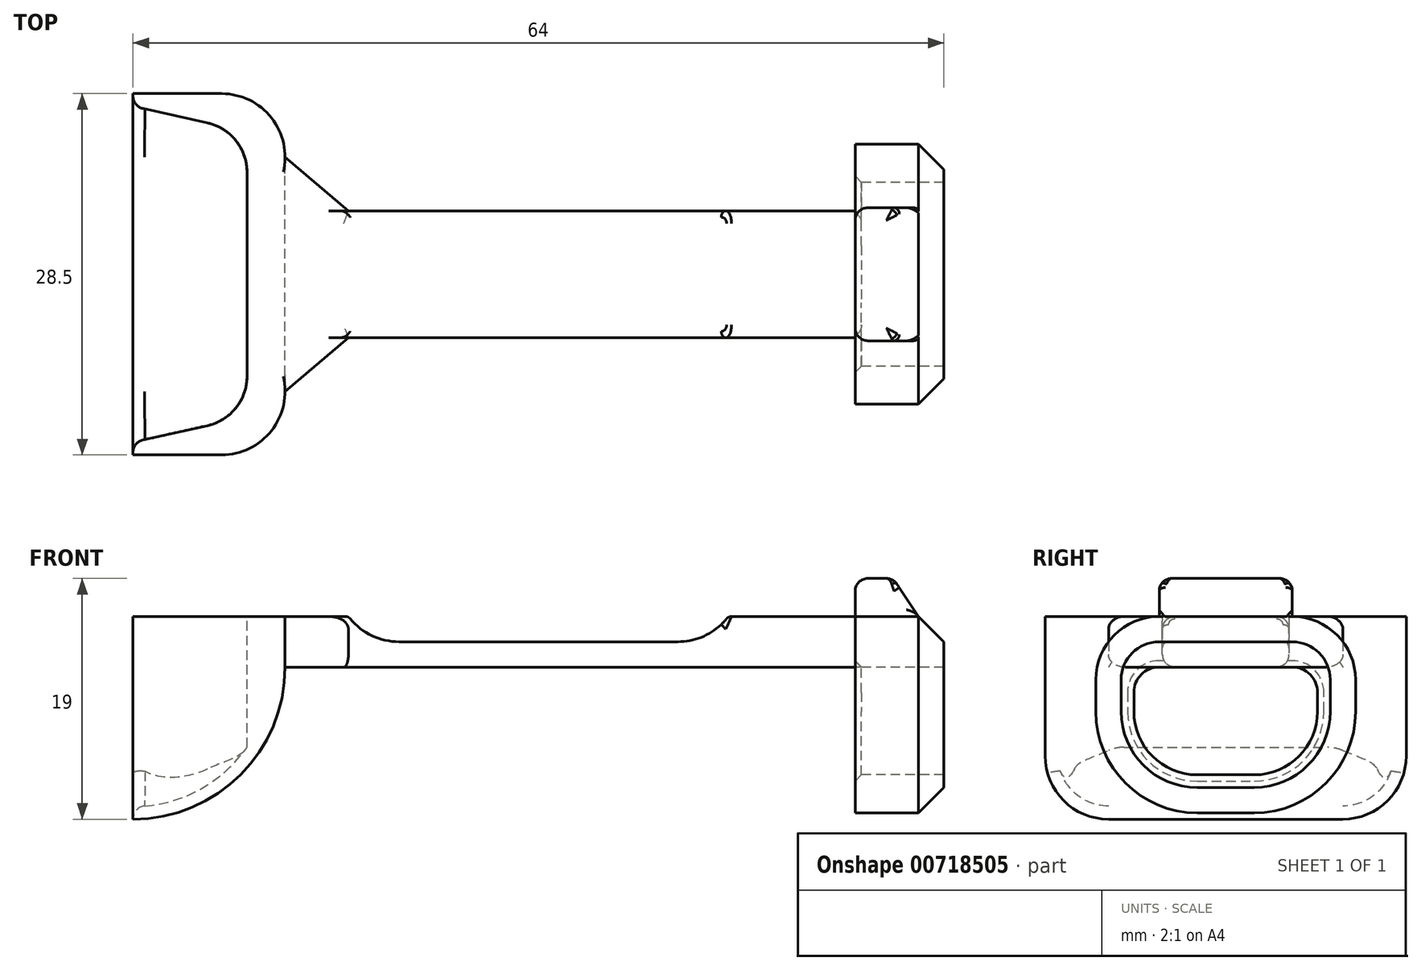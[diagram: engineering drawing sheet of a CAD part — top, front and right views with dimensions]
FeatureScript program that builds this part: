
annotation { "Feature Type Name" : "Feature", "Feature Type Description" : "" }
export const myFeature = defineFeature(function(context is Context, id is Id, definition is map)
    precondition{}
    {
        {
            assignVariable(context, id + "F0", {"variableType" : VariableType.LENGTH, "name" : "ScoopHeight", "lengthValue" : 12 * mm});
        }
        {
            assignVariable(context, id + "F1", {"variableType" : VariableType.LENGTH, "name" : "Length", "lengthValue" : 40 * mm});
        }
        {
            assignVariable(context, id + "F2", {"variableType" : VariableType.LENGTH, "name" : "OverHeight", "lengthValue" : 4 * mm});
        }
        {
            assignVariable(context, id + "F3", {"variableType" : VariableType.LENGTH, "name" : "BraceLength", "lengthValue" : 7 * mm});
        }
        {
            assignVariable(context, id + "F4", {"variableType" : VariableType.LENGTH, "name" : "StartLength", "lengthValue" : 5 * mm});
        }
        {
            var Q0;
            Q0=qCreatedBy(makeId("Right.planeOp"),FACE);
            var sketch = newSketch(context, id + "F5", { "sketchPlane" : qUnion([Q0])});
            skLineSegment(sketch, "E0", {"start": v(0, 0) * mm, "end": v(9.25, 0) * mm});
            skLineSegment(sketch, "E1", {"start": v(14.25, 5) * mm, "end": v(14.25, 12) * mm});
            skLineSegment(sketch, "E2", {"start": v(14.25, 12) * mm, "end": v(13.25, 12) * mm});
            skLineSegment(sketch, "E3", {"start": v(13.25, 12) * mm, "end": v(13.25, 5) * mm});
            skLineSegment(sketch, "E4", {"start": v(9.25, 1) * mm, "end": v(-9.25, 1) * mm});
            skLineSegment(sketch, "E5", {"start": v(-13.25, 5) * mm, "end": v(-13.25, 12) * mm});
            skLineSegment(sketch, "E6", {"start": v(-13.25, 12) * mm, "end": v(-14.25, 12) * mm});
            skLineSegment(sketch, "E7", {"start": v(-14.25, 12) * mm, "end": v(-14.25, 5) * mm});
            skLineSegment(sketch, "E8", {"start": v(-9.25, 0) * mm, "end": v(0, 0) * mm});
            skLineSegment(sketch, "E9", {"start": v(3.93, 12) * mm, "end": v(-6.74, 12) * mm});
            skPoint(sketch, "E10.visualSharp", {"position": v(13.25, 1) * mm});
            skArc(sketch, "E10.filletArc", {"start": v(9.25, 1) * mm, "mid": v(12.08, 2.17) * mm, "end": v(13.25, 5) * mm});
            skPoint(sketch, "E11.visualSharp", {"position": v(-13.25, 1) * mm});
            skArc(sketch, "E11.filletArc", {"start": v(-13.25, 5) * mm, "mid": v(-12.08, 2.17) * mm, "end": v(-9.25, 1) * mm});
            skPoint(sketch, "E12.visualSharp", {"position": v(-14.25, 0) * mm});
            skArc(sketch, "E12.filletArc", {"start": v(-14.25, 5) * mm, "mid": v(-12.79, 1.46) * mm, "end": v(-9.25, 0) * mm});
            skPoint(sketch, "E13.visualSharp", {"position": v(14.25, 0) * mm});
            skArc(sketch, "E13.filletArc", {"start": v(9.25, 0) * mm, "mid": v(12.79, 1.46) * mm, "end": v(14.25, 5) * mm});
            skSolve(sketch);
        }
        {
            var Q0;
            Q0=makeQuery(id+"F5.imprint","IMPRINT",FACE,{"disambiguationData":[TD([[makeQuery(id+"F5.imprint","IMPRINT",EDGE,{"derivedFrom":sQuery(id+"F5.wireOp",EDGE,"E0")}),1.0]])]});
            var Q1;
            Q1=sQuery(id+"F5.wireOp",EDGE,"E9");
            revolve(context, id + "F6", {"surfaceOperationType" : NewSurfaceOperationType.NEW, "entities" : qUnion([Q0]), "axis" : qUnion([Q1]), "revolveType" : RevolveType.ONE_DIRECTION, "angle" : 90 * degree});
        }
        {
            var Q0;
            Q0=makeQuery(id+"F6.opRevolve","CAP_FACE",FACE,{"disambiguationData":[OSD([sQuery(id+"F5.wireOp",EDGE,"E0"),sQuery(id+"F5.wireOp",EDGE,"E1"),sQuery(id+"F5.wireOp",EDGE,"E2"),sQuery(id+"F5.wireOp",EDGE,"E3"),sQuery(id+"F5.wireOp",EDGE,"E4"),sQuery(id+"F5.wireOp",EDGE,"E5"),sQuery(id+"F5.wireOp",EDGE,"E6"),sQuery(id+"F5.wireOp",EDGE,"E7"),sQuery(id+"F5.wireOp",EDGE,"E8"),sQuery(id+"F5.wireOp",EDGE,"E10.filletArc"),sQuery(id+"F5.wireOp",EDGE,"E11.filletArc"),sQuery(id+"F5.wireOp",EDGE,"E12.filletArc"),sQuery(id+"F5.wireOp",EDGE,"E13.filletArc")])],"isStart":false});
            var sketch = newSketch(context, id + "F7", { "sketchPlane" : qUnion([Q0])});
            skLineSegment(sketch, "E14", {"start": v(9, -8.04) * mm, "end": v(9, 8.04) * mm});
            skLineSegment(sketch, "E15", {"start": v(5.87, -11.95) * mm, "end": v(0, -13.25) * mm});
            skLineSegment(sketch, "E16", {"start": v(5.87, 11.95) * mm, "end": v(0, 13.25) * mm});
            skPoint(sketch, "E17.visualSharp", {"position": v(9, 11.25) * mm});
            skArc(sketch, "E17.filletArc", {"start": v(9, 8.04) * mm, "mid": v(8.12, 10.54) * mm, "end": v(5.87, 11.95) * mm});
            skPoint(sketch, "E18.visualSharp", {"position": v(9, -11.25) * mm});
            skArc(sketch, "E18.filletArc", {"start": v(5.87, -11.95) * mm, "mid": v(8.12, -10.54) * mm, "end": v(9, -8.04) * mm});
            skSolve(sketch);
        }
        {
            var Q0;
            Q0=makeQuery(id+"F7.imprint","IMPRINT",FACE,{"disambiguationData":[TD([[makeQuery(id+"F7.imprint","IMPRINT",EDGE,{"derivedFrom":sQuery(id+"F7.wireOp",EDGE,"E14")}),-1.0]])]});
            extrude(context, id + "F8", {"entities" : qUnion([Q0]), "operationType" : NewBodyOperationType.ADD, "oppositeDirection" : true, "depth" : 4 * mm, "offsetDistance" : 25 * mm});
        }
        {
            var Q0;
            Q0=makeQuery(id+"F8.opExtrude","CAP_FACE",FACE,{"disambiguationData":[OSD([sQuery(id+"F5.wireOp",EDGE,"E3"),sQuery(id+"F5.wireOp",EDGE,"E4"),sQuery(id+"F5.wireOp",EDGE,"E5"),sQuery(id+"F5.wireOp",EDGE,"E10.filletArc"),sQuery(id+"F5.wireOp",EDGE,"E11.filletArc"),sQuery(id+"F7.wireOp",EDGE,"E14"),sQuery(id+"F7.wireOp",EDGE,"E15"),sQuery(id+"F7.wireOp",EDGE,"E16"),sQuery(id+"F7.wireOp",EDGE,"E17.filletArc"),sQuery(id+"F7.wireOp",EDGE,"E18.filletArc")])],"isStart":false});
            extrude(context, id + "F9", {"entities" : qUnion([Q0]), "operationType" : NewBodyOperationType.ADD, "depth" : 2 * mm, "offsetDistance" : 25 * mm});
        }
        {
            var Q0;
            Q0=makeQuery(id+"F9.opExtrude","CAP_FACE",FACE,{"disambiguationData":[OSD([sQuery(id+"F5.wireOp",EDGE,"E3"),sQuery(id+"F5.wireOp",EDGE,"E4"),sQuery(id+"F5.wireOp",EDGE,"E5"),sQuery(id+"F5.wireOp",EDGE,"E10.filletArc"),sQuery(id+"F5.wireOp",EDGE,"E11.filletArc"),sQuery(id+"F7.wireOp",EDGE,"E14"),sQuery(id+"F7.wireOp",EDGE,"E15"),sQuery(id+"F7.wireOp",EDGE,"E16"),sQuery(id+"F7.wireOp",EDGE,"E17.filletArc"),sQuery(id+"F7.wireOp",EDGE,"E18.filletArc")])],"isStart":false});
            extrude(context, id + "F10", {"entities" : qUnion([Q0]), "operationType" : NewBodyOperationType.ADD, "depth" : 1.5 * mm, "offsetDistance" : 25 * mm});
        }
        {
            var Q0;
            {var subQ0=sQuery(id+"F7.wireOp",EDGE,"E16");var subQ1=sQuery(id+"F7.wireOp",EDGE,"E17.filletArc");var subQ2=sQuery(id+"F5.wireOp",EDGE,"E10.filletArc");Q0=makeQuery(id+"F10.boolean.opBoolean","SPLIT",FACE,{"disambiguationData":[TD([makeQuery(id+"F6.opRevolve","SWEPT_FACE",FACE,{"disambiguationData":[OSD([subQ2])]})])],"derivedFrom":makeQuery(id+"F10.opExtrude","CAP_FACE",FACE,{"disambiguationData":[OSD([sQuery(id+"F5.wireOp",EDGE,"E3"),sQuery(id+"F5.wireOp",EDGE,"E4"),sQuery(id+"F5.wireOp",EDGE,"E5"),subQ2,sQuery(id+"F5.wireOp",EDGE,"E11.filletArc"),sQuery(id+"F7.wireOp",EDGE,"E14"),sQuery(id+"F7.wireOp",EDGE,"E15"),subQ0,subQ1,sQuery(id+"F7.wireOp",EDGE,"E18.filletArc")])],"isStart":false})});}
            var Q1;
            {var subQ0=sQuery(id+"F7.wireOp",EDGE,"E15");var subQ1=sQuery(id+"F7.wireOp",EDGE,"E18.filletArc");var subQ2=sQuery(id+"F5.wireOp",EDGE,"E11.filletArc");Q1=makeQuery(id+"F10.boolean.opBoolean","SPLIT",FACE,{"disambiguationData":[TD([makeQuery(id+"F6.opRevolve","SWEPT_FACE",FACE,{"disambiguationData":[OSD([subQ2])]})])],"derivedFrom":makeQuery(id+"F10.opExtrude","CAP_FACE",FACE,{"disambiguationData":[OSD([sQuery(id+"F5.wireOp",EDGE,"E3"),sQuery(id+"F5.wireOp",EDGE,"E4"),sQuery(id+"F5.wireOp",EDGE,"E5"),sQuery(id+"F5.wireOp",EDGE,"E10.filletArc"),subQ2,sQuery(id+"F7.wireOp",EDGE,"E14"),subQ0,sQuery(id+"F7.wireOp",EDGE,"E16"),sQuery(id+"F7.wireOp",EDGE,"E17.filletArc"),subQ1])],"isStart":false})});}
            extrude(context, id + "F11", {"entities" : qUnion([Q0, Q1]), "operationType" : NewBodyOperationType.ADD, "depth" : 1.5 * mm, "offsetDistance" : 25 * mm});
        }
        {
            var Q0;
            {var subQ0=sQuery(id+"F5.wireOp",EDGE,"E11.filletArc");var subQ1=sQuery(id+"F5.wireOp",EDGE,"E10.filletArc");var subQ2=sQuery(id+"F5.wireOp",EDGE,"E5");var subQ3=sQuery(id+"F5.wireOp",EDGE,"E4");var subQ4=sQuery(id+"F5.wireOp",EDGE,"E3");Q0=makeQuery(id+"F8.boolean.opBoolean","MERGE",FACE,{"derivedFrom":[makeQuery(id+"F6.opRevolve","CAP_FACE",FACE,{"disambiguationData":[OSD([sQuery(id+"F5.wireOp",EDGE,"E0"),sQuery(id+"F5.wireOp",EDGE,"E1"),sQuery(id+"F5.wireOp",EDGE,"E2"),subQ4,subQ3,subQ2,sQuery(id+"F5.wireOp",EDGE,"E6"),sQuery(id+"F5.wireOp",EDGE,"E7"),sQuery(id+"F5.wireOp",EDGE,"E8"),subQ1,subQ0,sQuery(id+"F5.wireOp",EDGE,"E12.filletArc"),sQuery(id+"F5.wireOp",EDGE,"E13.filletArc")])],"isStart":false}),makeQuery(id+"F8.opExtrude","CAP_FACE",FACE,{"disambiguationData":[OSD([subQ4,subQ3,subQ2,subQ1,subQ0,sQuery(id+"F7.wireOp",EDGE,"E14"),sQuery(id+"F7.wireOp",EDGE,"E15"),sQuery(id+"F7.wireOp",EDGE,"E16"),sQuery(id+"F7.wireOp",EDGE,"E17.filletArc"),sQuery(id+"F7.wireOp",EDGE,"E18.filletArc")])],"isStart":true})]});}
            extrude(context, id + "F12", {"entities" : qUnion([Q0]), "operationType" : NewBodyOperationType.ADD, "depth" : getVariable(context, 'OverHeight'), "offsetDistance" : 25 * mm});
        }
        {
            var Q0;
            Q0=qCreatedBy(makeId("Right.planeOp"),FACE);
            cPlane(context, id + "F13", {"entities" : qUnion([Q0]), "cplaneType" : CPlaneType.OFFSET, "offset" : getVariable(context, 'StartLength') + getVariable(context, 'ScoopHeight'), "width" : 150 * mm, "height" : 150 * mm});
        }
        {
            var Q0;
            Q0=qCreatedBy(id+"F13.planeOp",FACE);
            var sketch = newSketch(context, id + "F14", { "sketchPlane" : qUnion([Q0])});
            skLineSegment(sketch, "E19", {"start": v(-5, 16) * mm, "end": v(5, 16) * mm});
            skLineSegment(sketch, "E20", {"start": v(5, 16) * mm, "end": v(5, 12) * mm});
            skLineSegment(sketch, "E21", {"start": v(5, 12) * mm, "end": v(-5, 12) * mm});
            skLineSegment(sketch, "E22", {"start": v(-5, 12) * mm, "end": v(-5, 16) * mm});
            skSolve(sketch);
        }
        {
            var Q0;
            Q0=makeQuery(id+"F12.opExtrude","SWEPT_FACE",FACE,{"disambiguationData":[OSD([sQuery(id+"F5.wireOp",EDGE,"E0"),sQuery(id+"F5.wireOp",EDGE,"E8")])]});
            var Q1;
            Q1=makeQuery(id+"F14.imprint","IMPRINT",FACE,{"disambiguationData":[TD([[makeQuery(id+"F14.imprint","IMPRINT",EDGE,{"derivedFrom":sQuery(id+"F14.wireOp",EDGE,"E19")}),-1.0]])]});
            loft(context, id + "F15", {"operationType" : NewBodyOperationType.ADD, "sheetProfilesArray" : [{ "sheetProfileEntities" : qUnion([Q0]) }, { "sheetProfileEntities" : qUnion([Q1]) }]});
        }
        {
            var Q0;
            Q0=makeQuery(id+"F15.opLoft","CAP_FACE",FACE,{"disambiguationData":[OSD([makeQuery(id+"F14.imprint","IMPRINT",FACE,{"disambiguationData":[TD([[makeQuery(id+"F14.imprint","IMPRINT",EDGE,{"derivedFrom":sQuery(id+"F14.wireOp",EDGE,"E19")}),-1.0]])]})])],"isStart":true});
            extrude(context, id + "F16", {"entities" : qUnion([Q0]), "operationType" : NewBodyOperationType.ADD, "depth" : getVariable(context, 'Length'), "offsetDistance" : 25 * mm});
        }
        {
            var Q0;
            Q0=makeQuery(id+"F16.opExtrude","CAP_FACE",FACE,{"disambiguationData":[OSD([makeQuery(id+"F14.imprint","IMPRINT",FACE,{"disambiguationData":[TD([[makeQuery(id+"F14.imprint","IMPRINT",EDGE,{"derivedFrom":sQuery(id+"F14.wireOp",EDGE,"E19")}),-1.0]])]})])],"isStart":false});
            var sketch = newSketch(context, id + "F17", { "sketchPlane" : qUnion([Q0])});
            skLineSegment(sketch, "E23", {"start": v(-10.25, 11) * mm, "end": v(-10.25, 8.5) * mm});
            skLineSegment(sketch, "E24", {"start": v(-2.25, 0.5) * mm, "end": v(2.25, 0.5) * mm});
            skLineSegment(sketch, "E25", {"start": v(10.25, 8.5) * mm, "end": v(10.25, 11) * mm});
            skLineSegment(sketch, "E26", {"start": v(5.25, 12) * mm, "end": v(-5.25, 12) * mm});
            skLineSegment(sketch, "E27", {"start": v(-7.25, 10) * mm, "end": v(-7.25, 8.5) * mm});
            skLineSegment(sketch, "E28", {"start": v(-2.25, 3.5) * mm, "end": v(2.25, 3.5) * mm});
            skLineSegment(sketch, "E29", {"start": v(7.25, 8.5) * mm, "end": v(7.25, 10) * mm});
            skPoint(sketch, "E30.visualSharp", {"position": v(-7.25, 12) * mm});
            skArc(sketch, "E30.filletArc", {"start": v(-5.25, 12) * mm, "mid": v(-6.66, 11.41) * mm, "end": v(-7.25, 10) * mm});
            skPoint(sketch, "E31.visualSharp", {"position": v(7.25, 12) * mm});
            skArc(sketch, "E31.filletArc", {"start": v(7.25, 10) * mm, "mid": v(6.66, 11.41) * mm, "end": v(5.25, 12) * mm});
            skPoint(sketch, "E32.visualSharp", {"position": v(7.25, 3.5) * mm});
            skArc(sketch, "E32.filletArc", {"start": v(2.25, 3.5) * mm, "mid": v(5.79, 4.96) * mm, "end": v(7.25, 8.5) * mm});
            skPoint(sketch, "E33.visualSharp", {"position": v(-7.25, 3.5) * mm});
            skArc(sketch, "E33.filletArc", {"start": v(-7.25, 8.5) * mm, "mid": v(-5.79, 4.96) * mm, "end": v(-2.25, 3.5) * mm});
            skLineSegment(sketch, "E34", {"start": v(5.25, 16) * mm, "end": v(-5.25, 16) * mm});
            skPoint(sketch, "E35.visualSharp", {"position": v(-10.25, 16) * mm});
            skArc(sketch, "E35.filletArc", {"start": v(-5.25, 16) * mm, "mid": v(-8.79, 14.54) * mm, "end": v(-10.25, 11) * mm});
            skPoint(sketch, "E36.visualSharp", {"position": v(10.25, 16) * mm});
            skArc(sketch, "E36.filletArc", {"start": v(10.25, 11) * mm, "mid": v(8.79, 14.54) * mm, "end": v(5.25, 16) * mm});
            skPoint(sketch, "E37.visualSharp", {"position": v(10.25, 0.5) * mm});
            skArc(sketch, "E37.filletArc", {"start": v(2.25, 0.5) * mm, "mid": v(7.9, 2.84) * mm, "end": v(10.25, 8.5) * mm});
            skPoint(sketch, "E38.visualSharp", {"position": v(-10.25, 0.5) * mm});
            skArc(sketch, "E38.filletArc", {"start": v(-10.25, 8.5) * mm, "mid": v(-7.9, 2.84) * mm, "end": v(-2.25, 0.5) * mm});
            skSolve(sketch);
        }
        {
            var Q0;
            {var subQ1=sQuery(id+"F14.wireOp",EDGE,"E21");var subQ2=sQuery(id+"F14.wireOp",EDGE,"E19");var subQ4=makeQuery(id+"F16.opExtrude","CAP_EDGE",EDGE,{"disambiguationData":[OSD([subQ2,subQ1,sQuery(id+"F14.wireOp",EDGE,"E22")])],"isStart":false});Q0=makeQuery(id+"F17.imprint","IMPRINT",FACE,{"disambiguationData":[TD([[makeQuery(id+"F17.imprint","IMPRINT",EDGE,{"derivedFrom":subQ4}),1.0]])]});}
            var Q1;
            Q1=makeQuery(id+"F17.imprint","IMPRINT",FACE,{"disambiguationData":[TD([[makeQuery(id+"F17.imprint","IMPRINT",EDGE,{"derivedFrom":sQuery(id+"F17.wireOp",EDGE,"E23")}),1.0]])]});
            extrude(context, id + "F18", {"entities" : qUnion([Q0, Q1]), "operationType" : NewBodyOperationType.ADD, "depth" : getVariable(context, 'BraceLength'), "offsetDistance" : 25 * mm});
        }
        {
            var Q0;
            {var subQ0=sQuery(id+"F14.wireOp",EDGE,"E22");var subQ1=sQuery(id+"F14.wireOp",EDGE,"E20");var subQ2=sQuery(id+"F14.wireOp",EDGE,"E19");var subQ3=sQuery(id+"F5.wireOp",EDGE,"E13.filletArc");var subQ4=sQuery(id+"F5.wireOp",EDGE,"E12.filletArc");var subQ5=sQuery(id+"F5.wireOp",EDGE,"E8");var subQ6=sQuery(id+"F5.wireOp",EDGE,"E0");Q0=makeQuery(id+"F18.boolean.opBoolean","MERGE",FACE,{"derivedFrom":[makeQuery(id+"F16.boolean.opBoolean","MERGE",FACE,{"derivedFrom":[makeQuery(id+"F15.boolean.opBoolean","MERGE",FACE,{"derivedFrom":[makeQuery(id+"F12.opExtrude","CAP_FACE",FACE,{"disambiguationData":[OSD([subQ6,sQuery(id+"F5.wireOp",EDGE,"E1"),sQuery(id+"F5.wireOp",EDGE,"E2"),sQuery(id+"F5.wireOp",EDGE,"E3"),sQuery(id+"F5.wireOp",EDGE,"E4"),sQuery(id+"F5.wireOp",EDGE,"E5"),sQuery(id+"F5.wireOp",EDGE,"E6"),sQuery(id+"F5.wireOp",EDGE,"E7"),subQ5,sQuery(id+"F5.wireOp",EDGE,"E10.filletArc"),sQuery(id+"F5.wireOp",EDGE,"E11.filletArc"),subQ4,subQ3,sQuery(id+"F7.wireOp",EDGE,"E14"),sQuery(id+"F7.wireOp",EDGE,"E15"),sQuery(id+"F7.wireOp",EDGE,"E16"),sQuery(id+"F7.wireOp",EDGE,"E17.filletArc"),sQuery(id+"F7.wireOp",EDGE,"E18.filletArc")])],"isStart":false}),makeQuery(id+"F15.opLoft","SWEPT_FACE",FACE,{"disambiguationData":[OSD([subQ6,subQ5,subQ4,subQ3,subQ2,subQ1,subQ0])]})]}),makeQuery(id+"F16.opExtrude","SWEPT_FACE",FACE,{"disambiguationData":[OSD([subQ2,subQ1,subQ0])]})]}),makeQuery(id+"F18.opExtrude","SWEPT_FACE",FACE,{"disambiguationData":[OSD([sQuery(id+"F17.wireOp",EDGE,"E34")])]})]});}
            var sketch = newSketch(context, id + "F19", { "sketchPlane" : qUnion([Q0])});
            skLineSegment(sketch, "E39", {"start": v(17, -5) * mm, "end": v(17, 5) * mm});
            skLineSegment(sketch, "E40", {"start": v(17, 5) * mm, "end": v(47, 5) * mm});
            skLineSegment(sketch, "E41", {"start": v(47, 5) * mm, "end": v(47, -5) * mm});
            skLineSegment(sketch, "E42", {"start": v(47, -5) * mm, "end": v(17, -5) * mm});
            skSolve(sketch);
        }
        {
            assignVariable(context, id + "F20", {"variableType" : VariableType.LENGTH, "name" : "FlexCutout", "lengthValue" : 2 * mm});
        }
        {
            var Q0;
            Q0=makeQuery(id+"F19.imprint","IMPRINT",FACE,{"disambiguationData":[TD([[makeQuery(id+"F19.imprint","IMPRINT",EDGE,{"derivedFrom":sQuery(id+"F19.wireOp",EDGE,"E39")}),-1.0]])]});
            extrude(context, id + "F21", {"entities" : qUnion([Q0]), "operationType" : NewBodyOperationType.REMOVE, "oppositeDirection" : true, "depth" : getVariable(context, 'FlexCutout'), "offsetDistance" : 25 * mm});
        }
        {
            var Q0;
            Q0=makeQuery(id+"F21.boolean.opBoolean","COPY",EDGE,{"derivedFrom":makeQuery(id+"F21.opExtrude","CAP_EDGE",EDGE,{"disambiguationData":[OSD([sQuery(id+"F19.wireOp",EDGE,"E41")])],"isStart":false})});
            var Q1;
            Q1=makeQuery(id+"F21.boolean.opBoolean","COPY",EDGE,{"derivedFrom":makeQuery(id+"F21.opExtrude","CAP_EDGE",EDGE,{"disambiguationData":[OSD([sQuery(id+"F19.wireOp",EDGE,"E39")])],"isStart":false})});
            fillet(context, id + "F22", {"entities" : qUnion([Q0, Q1]), "tangentPropagation" : true, "radius" : 5 * mm, "defaultsChanged" : false, "vertexSettings" : []});
        }
        {
            var Q0;
            Q0=makeQuery(id+"F16.opExtrude","SWEPT_EDGE",EDGE,{"disambiguationData":[OSD([sQuery(id+"F14.wireOp",EDGE,"E19"),sQuery(id+"F14.wireOp",EDGE,"E22")])]});
            var Q1;
            Q1=makeQuery(id+"F16.opExtrude","SWEPT_EDGE",EDGE,{"disambiguationData":[OSD([sQuery(id+"F14.wireOp",EDGE,"E19"),sQuery(id+"F14.wireOp",EDGE,"E20")])]});
            var Q2;
            Q2=makeQuery(id+"F16.opExtrude","SWEPT_EDGE",EDGE,{"disambiguationData":[OSD([sQuery(id+"F14.wireOp",EDGE,"E20"),sQuery(id+"F14.wireOp",EDGE,"E21")])]});
            var Q3;
            Q3=makeQuery(id+"F16.opExtrude","SWEPT_EDGE",EDGE,{"disambiguationData":[OSD([sQuery(id+"F14.wireOp",EDGE,"E21"),sQuery(id+"F14.wireOp",EDGE,"E22")])]});
            var Q4;
            Q4=makeQuery(id+"F15.opLoft","SWEPT_EDGE",EDGE,{"disambiguationData":[OSD([sQuery(id+"F5.wireOp",EDGE,"E8"),sQuery(id+"F5.wireOp",EDGE,"E12.filletArc"),sQuery(id+"F14.wireOp",EDGE,"E19"),sQuery(id+"F14.wireOp",EDGE,"E22")])]});
            var Q5;
            Q5=makeQuery(id+"F15.opLoft","SWEPT_EDGE",EDGE,{"disambiguationData":[OSD([sQuery(id+"F5.wireOp",EDGE,"E8"),sQuery(id+"F5.wireOp",EDGE,"E12.filletArc"),sQuery(id+"F14.wireOp",EDGE,"E21"),sQuery(id+"F14.wireOp",EDGE,"E22")])]});
            var Q6;
            Q6=makeQuery(id+"F15.opLoft","SWEPT_EDGE",EDGE,{"disambiguationData":[OSD([sQuery(id+"F5.wireOp",EDGE,"E0"),sQuery(id+"F5.wireOp",EDGE,"E13.filletArc"),sQuery(id+"F14.wireOp",EDGE,"E19"),sQuery(id+"F14.wireOp",EDGE,"E20")])]});
            var Q7;
            Q7=makeQuery(id+"F15.opLoft","SWEPT_EDGE",EDGE,{"disambiguationData":[OSD([sQuery(id+"F5.wireOp",EDGE,"E0"),sQuery(id+"F5.wireOp",EDGE,"E13.filletArc"),sQuery(id+"F14.wireOp",EDGE,"E20"),sQuery(id+"F14.wireOp",EDGE,"E21")])]});
            var Q8;
            {var subQ0=sQuery(id+"F7.wireOp",EDGE,"E15");var subQ1=sQuery(id+"F5.wireOp",EDGE,"E6");var subQ2=sQuery(id+"F5.wireOp",EDGE,"E5");var subQ3=makeQuery(id+"F6.opRevolve","CAP_EDGE",EDGE,{"disambiguationData":[OSD([subQ2])],"isStart":true});var subQ4=makeQuery(id+"F8.boolean.opBoolean","SPLIT",EDGE,{"derivedFrom":subQ3});Q8=makeQuery(id+"F12.boolean.opBoolean","MERGE",EDGE,{"derivedFrom":[makeQuery(id+"F10.boolean.opBoolean","MERGE",EDGE,{"derivedFrom":[makeQuery(id+"F9.boolean.opBoolean","MERGE",EDGE,{"derivedFrom":[makeQuery(id+"F8.boolean.opBoolean","MERGE",EDGE,{"derivedFrom":[subQ3,makeQuery(id+"F8.opExtrude","SWEPT_EDGE",EDGE,{"disambiguationData":[OSD([subQ2,subQ1,subQ0])]})]}),subQ4,makeQuery(id+"F9.opExtrude","SWEPT_EDGE",EDGE,{"disambiguationData":[OSD([subQ2,subQ1,subQ0])]})]}),makeQuery(id+"F9.boolean.opBoolean","SPLIT",EDGE,{"derivedFrom":subQ4}),makeQuery(id+"F10.opExtrude","SWEPT_EDGE",EDGE,{"disambiguationData":[OSD([subQ2,subQ1,subQ0])]})]}),makeQuery(id+"F12.opExtrude","SWEPT_EDGE",EDGE,{"disambiguationData":[OSD([subQ2,subQ1,subQ0])]})]});}
            var Q9;
            Q9=makeQuery(id+"F6.opRevolve","CAP_EDGE",EDGE,{"disambiguationData":[OSD([sQuery(id+"F5.wireOp",EDGE,"E4")])],"isStart":true});
            var Q10;
            {var subQ0=sQuery(id+"F7.wireOp",EDGE,"E16");var subQ1=sQuery(id+"F5.wireOp",EDGE,"E3");var subQ2=sQuery(id+"F5.wireOp",EDGE,"E2");var subQ3=makeQuery(id+"F6.opRevolve","CAP_EDGE",EDGE,{"disambiguationData":[OSD([subQ1])],"isStart":true});var subQ4=makeQuery(id+"F8.boolean.opBoolean","SPLIT",EDGE,{"derivedFrom":subQ3});Q10=makeQuery(id+"F12.boolean.opBoolean","MERGE",EDGE,{"derivedFrom":[makeQuery(id+"F10.boolean.opBoolean","MERGE",EDGE,{"derivedFrom":[makeQuery(id+"F9.boolean.opBoolean","MERGE",EDGE,{"derivedFrom":[makeQuery(id+"F8.boolean.opBoolean","MERGE",EDGE,{"derivedFrom":[subQ3,makeQuery(id+"F8.opExtrude","SWEPT_EDGE",EDGE,{"disambiguationData":[OSD([subQ2,subQ1,subQ0])]})]}),subQ4,makeQuery(id+"F9.opExtrude","SWEPT_EDGE",EDGE,{"disambiguationData":[OSD([subQ2,subQ1,subQ0])]})]}),makeQuery(id+"F9.boolean.opBoolean","SPLIT",EDGE,{"derivedFrom":subQ4}),makeQuery(id+"F10.opExtrude","SWEPT_EDGE",EDGE,{"disambiguationData":[OSD([subQ2,subQ1,subQ0])]})]}),makeQuery(id+"F12.opExtrude","SWEPT_EDGE",EDGE,{"disambiguationData":[OSD([subQ2,subQ1,subQ0])]})]});}
            fillet(context, id + "F23", {"entities" : qUnion([Q0, Q1, Q2, Q3, Q4, Q5, Q6, Q7, Q8, Q9, Q10]), "tangentPropagation" : true, "radius" : 1 * mm, "defaultsChanged" : false, "vertexSettings" : []});
        }
        {
            var Q0;
            Q0=makeQuery(id+"F18.opExtrude","CAP_EDGE",EDGE,{"disambiguationData":[OSD([sQuery(id+"F17.wireOp",EDGE,"E34")])],"isStart":false});
            chamfer(context, id + "F24", {"entities" : qUnion([Q0]), "width" : 2 * mm, "tangentPropagation" : true});
        }
        {
            var Q0;
            {var subQ0=sQuery(id+"F14.wireOp",EDGE,"E22");var subQ1=sQuery(id+"F14.wireOp",EDGE,"E20");var subQ2=sQuery(id+"F14.wireOp",EDGE,"E19");var subQ3=sQuery(id+"F5.wireOp",EDGE,"E13.filletArc");var subQ4=sQuery(id+"F5.wireOp",EDGE,"E12.filletArc");var subQ5=sQuery(id+"F5.wireOp",EDGE,"E8");var subQ6=sQuery(id+"F5.wireOp",EDGE,"E0");Q0=makeQuery(id+"F18.boolean.opBoolean","MERGE",FACE,{"derivedFrom":[makeQuery(id+"F16.boolean.opBoolean","MERGE",FACE,{"derivedFrom":[makeQuery(id+"F15.boolean.opBoolean","MERGE",FACE,{"derivedFrom":[makeQuery(id+"F12.opExtrude","CAP_FACE",FACE,{"disambiguationData":[OSD([subQ6,sQuery(id+"F5.wireOp",EDGE,"E1"),sQuery(id+"F5.wireOp",EDGE,"E2"),sQuery(id+"F5.wireOp",EDGE,"E3"),sQuery(id+"F5.wireOp",EDGE,"E4"),sQuery(id+"F5.wireOp",EDGE,"E5"),sQuery(id+"F5.wireOp",EDGE,"E6"),sQuery(id+"F5.wireOp",EDGE,"E7"),subQ5,sQuery(id+"F5.wireOp",EDGE,"E10.filletArc"),sQuery(id+"F5.wireOp",EDGE,"E11.filletArc"),subQ4,subQ3,sQuery(id+"F7.wireOp",EDGE,"E14"),sQuery(id+"F7.wireOp",EDGE,"E15"),sQuery(id+"F7.wireOp",EDGE,"E16"),sQuery(id+"F7.wireOp",EDGE,"E17.filletArc"),sQuery(id+"F7.wireOp",EDGE,"E18.filletArc")])],"isStart":false}),makeQuery(id+"F15.opLoft","SWEPT_FACE",FACE,{"disambiguationData":[OSD([subQ6,subQ5,subQ4,subQ3,subQ2,subQ1,subQ0])]})]}),makeQuery(id+"F16.opExtrude","SWEPT_FACE",FACE,{"disambiguationData":[OSD([subQ2,subQ1,subQ0])]})]}),makeQuery(id+"F18.opExtrude","SWEPT_FACE",FACE,{"disambiguationData":[OSD([sQuery(id+"F17.wireOp",EDGE,"E34")])]})]});}
            var sketch = newSketch(context, id + "F25", { "sketchPlane" : qUnion([Q0])});
            skLineSegment(sketch, "E43", {"start": v(57, -5.25) * mm, "end": v(57, 5.25) * mm});
            skLineSegment(sketch, "E44", {"start": v(57, 5.25) * mm, "end": v(62, 5.25) * mm});
            skLineSegment(sketch, "E45", {"start": v(62, 5.25) * mm, "end": v(62, -5.25) * mm});
            skLineSegment(sketch, "E46", {"start": v(62, -5.25) * mm, "end": v(57, -5.25) * mm});
            skSolve(sketch);
        }
        {
            var Q0;
            Q0=makeQuery(id+"F25.imprint","IMPRINT",FACE,{"disambiguationData":[TD([[makeQuery(id+"F25.imprint","IMPRINT",EDGE,{"derivedFrom":sQuery(id+"F25.wireOp",EDGE,"E43")}),-1.0]])]});
            extrude(context, id + "F26", {"entities" : qUnion([Q0]), "operationType" : NewBodyOperationType.ADD, "depth" : 3 * mm, "offsetDistance" : 25 * mm});
        }
        {
            var Q0;
            Q0=makeQuery(id+"F26.opExtrude","CAP_EDGE",EDGE,{"disambiguationData":[OSD([sQuery(id+"F25.wireOp",EDGE,"E45")])],"isStart":false});
            chamfer(context, id + "F27", {"entities" : qUnion([Q0]), "chamferType" : ChamferType.TWO_OFFSETS, "width1" : 2 * mm, "oppositeDirection" : false, "width2" : 3 * mm});
        }
        {
            var Q0;
            {var subQ0=sQuery(id+"F25.wireOp",EDGE,"E45");Q0=makeQuery(id+"F27.opChamfer","BLEND_EDGE",EDGE,{"blendedFrom":[makeQuery(id+"F26.opExtrude","CAP_EDGE",EDGE,{"disambiguationData":[OSD([subQ0])],"isStart":false}),makeQuery(id+"F26.opExtrude","CAP_FACE",FACE,{"disambiguationData":[OSD([sQuery(id+"F25.wireOp",EDGE,"E43"),sQuery(id+"F25.wireOp",EDGE,"E44"),subQ0,sQuery(id+"F25.wireOp",EDGE,"E46")])],"isStart":false})],"blendedInto":[makeQuery(id+"F26.opExtrude","CAP_FACE",FACE,{"disambiguationData":[OSD([sQuery(id+"F25.wireOp",EDGE,"E43"),sQuery(id+"F25.wireOp",EDGE,"E44"),subQ0,sQuery(id+"F25.wireOp",EDGE,"E46")])],"isStart":false})]});}
            var Q1;
            Q1=makeQuery(id+"F26.opExtrude","CAP_EDGE",EDGE,{"disambiguationData":[OSD([sQuery(id+"F25.wireOp",EDGE,"E44")])],"isStart":false});
            var Q2;
            Q2=makeQuery(id+"F26.opExtrude","SWEPT_EDGE",EDGE,{"disambiguationData":[OSD([sQuery(id+"F14.wireOp",EDGE,"E19"),sQuery(id+"F14.wireOp",EDGE,"E20"),sQuery(id+"F14.wireOp",EDGE,"E22"),sQuery(id+"F25.wireOp",EDGE,"E43"),sQuery(id+"F25.wireOp",EDGE,"E44")])]});
            var Q3;
            Q3=makeQuery(id+"F26.opExtrude","CAP_EDGE",EDGE,{"disambiguationData":[OSD([sQuery(id+"F25.wireOp",EDGE,"E43")])],"isStart":false});
            var Q4;
            Q4=makeQuery(id+"F26.opExtrude","CAP_EDGE",EDGE,{"disambiguationData":[OSD([sQuery(id+"F25.wireOp",EDGE,"E46")])],"isStart":false});
            var Q5;
            Q5=makeQuery(id+"F26.opExtrude","SWEPT_EDGE",EDGE,{"disambiguationData":[OSD([sQuery(id+"F14.wireOp",EDGE,"E19"),sQuery(id+"F14.wireOp",EDGE,"E20"),sQuery(id+"F14.wireOp",EDGE,"E22"),sQuery(id+"F25.wireOp",EDGE,"E43"),sQuery(id+"F25.wireOp",EDGE,"E46")])]});
            fillet(context, id + "F28", {"entities" : qUnion([Q0, Q1, Q2, Q3, Q4, Q5]), "tangentPropagation" : true, "radius" : 1 * mm, "defaultsChanged" : false, "vertexSettings" : []});
        }
        {
            var Q0;
            Q0=makeQuery(id+"F27.opChamfer","BLEND_EDGE",EDGE,{"blendedFrom":[makeQuery(id+"F26.opExtrude","CAP_EDGE",EDGE,{"disambiguationData":[OSD([sQuery(id+"F25.wireOp",EDGE,"E45")])],"isStart":false}),makeQuery(id+"F26.opExtrude","SWEPT_FACE",FACE,{"disambiguationData":[OSD([sQuery(id+"F25.wireOp",EDGE,"E44")])]})],"blendedInto":[makeQuery(id+"F26.opExtrude","SWEPT_FACE",FACE,{"disambiguationData":[OSD([sQuery(id+"F25.wireOp",EDGE,"E44")])]})]});
            var Q1;
            Q1=makeQuery(id+"F27.opChamfer","BLEND_EDGE",EDGE,{"blendedFrom":[makeQuery(id+"F26.opExtrude","CAP_EDGE",EDGE,{"disambiguationData":[OSD([sQuery(id+"F25.wireOp",EDGE,"E45")])],"isStart":false}),makeQuery(id+"F26.opExtrude","SWEPT_FACE",FACE,{"disambiguationData":[OSD([sQuery(id+"F25.wireOp",EDGE,"E46")])]})],"blendedInto":[makeQuery(id+"F26.opExtrude","SWEPT_FACE",FACE,{"disambiguationData":[OSD([sQuery(id+"F25.wireOp",EDGE,"E46")])]})]});
            fillet(context, id + "F29", {"entities" : qUnion([Q0, Q1]), "tangentPropagation" : true, "radius" : 0.5 * mm, "defaultsChanged" : false, "vertexSettings" : []});
        }
        {
            var Q0;
            {var subQ0=sQuery(id+"F17.wireOp",EDGE,"E36.filletArc");Q0=makeQuery(id+"F29.opFillet","TWEAK_EDGE",EDGE,{"derivedFrom":[makeQuery(id+"F27.opChamfer","BLEND_VERTEX",VERTEX,{"blendedFrom":[makeQuery(id+"F26.opExtrude","CAP_EDGE",EDGE,{"disambiguationData":[OSD([sQuery(id+"F25.wireOp",EDGE,"E45")])],"isStart":false}),makeQuery(id+"F24.opChamfer","BLEND_FACE",FACE,{"disambiguationData":[OSD([sQuery(id+"F17.wireOp",EDGE,"E34")])]}),makeQuery(id+"F24.opChamfer","BLEND_FACE",FACE,{"disambiguationData":[OSD([subQ0])]}),makeQuery(id+"F18.opExtrude","SWEPT_FACE",FACE,{"disambiguationData":[OSD([subQ0])]}),makeQuery(id+"F26.opExtrude","SWEPT_FACE",FACE,{"disambiguationData":[OSD([sQuery(id+"F25.wireOp",EDGE,"E44")])]})],"blendedInto":[makeQuery(id+"F24.opChamfer","BLEND_FACE",FACE,{"disambiguationData":[OSD([sQuery(id+"F17.wireOp",EDGE,"E34")])]}),makeQuery(id+"F24.opChamfer","BLEND_FACE",FACE,{"disambiguationData":[OSD([subQ0])]}),makeQuery(id+"F18.opExtrude","SWEPT_FACE",FACE,{"disambiguationData":[OSD([subQ0])]}),makeQuery(id+"F26.opExtrude","SWEPT_FACE",FACE,{"disambiguationData":[OSD([sQuery(id+"F25.wireOp",EDGE,"E44")])]})]})]});}
            var Q1;
            {var subQ0=sQuery(id+"F17.wireOp",EDGE,"E35.filletArc");Q1=makeQuery(id+"F29.opFillet","TWEAK_EDGE",EDGE,{"derivedFrom":[makeQuery(id+"F27.opChamfer","BLEND_VERTEX",VERTEX,{"blendedFrom":[makeQuery(id+"F26.opExtrude","CAP_EDGE",EDGE,{"disambiguationData":[OSD([sQuery(id+"F25.wireOp",EDGE,"E45")])],"isStart":false}),makeQuery(id+"F24.opChamfer","BLEND_FACE",FACE,{"disambiguationData":[OSD([sQuery(id+"F17.wireOp",EDGE,"E34")])]}),makeQuery(id+"F24.opChamfer","BLEND_FACE",FACE,{"disambiguationData":[OSD([subQ0])]}),makeQuery(id+"F18.opExtrude","SWEPT_FACE",FACE,{"disambiguationData":[OSD([subQ0])]}),makeQuery(id+"F26.opExtrude","SWEPT_FACE",FACE,{"disambiguationData":[OSD([sQuery(id+"F25.wireOp",EDGE,"E46")])]})],"blendedInto":[makeQuery(id+"F24.opChamfer","BLEND_FACE",FACE,{"disambiguationData":[OSD([sQuery(id+"F17.wireOp",EDGE,"E34")])]}),makeQuery(id+"F24.opChamfer","BLEND_FACE",FACE,{"disambiguationData":[OSD([subQ0])]}),makeQuery(id+"F18.opExtrude","SWEPT_FACE",FACE,{"disambiguationData":[OSD([subQ0])]}),makeQuery(id+"F26.opExtrude","SWEPT_FACE",FACE,{"disambiguationData":[OSD([sQuery(id+"F25.wireOp",EDGE,"E46")])]})]})]});}
            fillet(context, id + "F30", {"entities" : qUnion([Q0, Q1]), "tangentPropagation" : true, "radius" : 0.3 * mm, "defaultsChanged" : false, "vertexSettings" : []});
        }
        {
            var Q0;
            Q0=makeQuery(id+"F18.opExtrude","CAP_EDGE",EDGE,{"disambiguationData":[OSD([sQuery(id+"F17.wireOp",EDGE,"E31.filletArc")])],"isStart":true});
            chamfer(context, id + "F31", {"entities" : qUnion([Q0]), "width" : 0.5 * mm, "tangentPropagation" : true});
        }
        {
            var Q0;
            {var subQ0=sQuery(id+"F14.wireOp",EDGE,"E19");var subQ1=sQuery(id+"F14.wireOp",EDGE,"E20");var subQ3=sQuery(id+"F14.wireOp",EDGE,"E22");var subQ5=sQuery(id+"F17.wireOp",EDGE,"E35.filletArc");var subQ6=sQuery(id+"F17.wireOp",EDGE,"E34");var subQ7=sQuery(id+"F19.wireOp",EDGE,"E41");var subQ8=sQuery(id+"F5.wireOp",EDGE,"E13.filletArc");var subQ9=sQuery(id+"F5.wireOp",EDGE,"E12.filletArc");var subQ10=sQuery(id+"F5.wireOp",EDGE,"E8");var subQ11=sQuery(id+"F5.wireOp",EDGE,"E0");Q0=makeQuery(id+"F22.opFillet","BLEND_EDGE",EDGE,{"blendedFrom":[makeQuery(id+"F21.boolean.opBoolean","COPY",EDGE,{"derivedFrom":makeQuery(id+"F21.opExtrude","CAP_EDGE",EDGE,{"disambiguationData":[OSD([subQ7])],"isStart":false})}),makeQuery(id+"F21.boolean.opBoolean","SPLIT",FACE,{"disambiguationData":[TD([makeQuery(id+"F18.opExtrude","SWEPT_FACE",FACE,{"disambiguationData":[OSD([subQ5])]})])],"derivedFrom":makeQuery(id+"F18.boolean.opBoolean","MERGE",FACE,{"derivedFrom":[makeQuery(id+"F16.boolean.opBoolean","MERGE",FACE,{"derivedFrom":[makeQuery(id+"F15.boolean.opBoolean","MERGE",FACE,{"derivedFrom":[makeQuery(id+"F12.opExtrude","CAP_FACE",FACE,{"disambiguationData":[OSD([subQ11,sQuery(id+"F5.wireOp",EDGE,"E1"),sQuery(id+"F5.wireOp",EDGE,"E2"),sQuery(id+"F5.wireOp",EDGE,"E3"),sQuery(id+"F5.wireOp",EDGE,"E4"),sQuery(id+"F5.wireOp",EDGE,"E5"),sQuery(id+"F5.wireOp",EDGE,"E6"),sQuery(id+"F5.wireOp",EDGE,"E7"),subQ10,sQuery(id+"F5.wireOp",EDGE,"E10.filletArc"),sQuery(id+"F5.wireOp",EDGE,"E11.filletArc"),subQ9,subQ8,sQuery(id+"F7.wireOp",EDGE,"E14"),sQuery(id+"F7.wireOp",EDGE,"E15"),sQuery(id+"F7.wireOp",EDGE,"E16"),sQuery(id+"F7.wireOp",EDGE,"E17.filletArc"),sQuery(id+"F7.wireOp",EDGE,"E18.filletArc")])],"isStart":false}),makeQuery(id+"F15.opLoft","SWEPT_FACE",FACE,{"disambiguationData":[OSD([subQ11,subQ10,subQ9,subQ8,subQ0,subQ1,subQ3])]})]}),makeQuery(id+"F16.opExtrude","SWEPT_FACE",FACE,{"disambiguationData":[OSD([subQ0,subQ1,subQ3])]})]}),makeQuery(id+"F18.opExtrude","SWEPT_FACE",FACE,{"disambiguationData":[OSD([subQ6])]})]})})],"blendedInto":[makeQuery(id+"F21.boolean.opBoolean","SPLIT",FACE,{"disambiguationData":[TD([makeQuery(id+"F18.opExtrude","SWEPT_FACE",FACE,{"disambiguationData":[OSD([subQ5])]})])],"derivedFrom":makeQuery(id+"F18.boolean.opBoolean","MERGE",FACE,{"derivedFrom":[makeQuery(id+"F16.boolean.opBoolean","MERGE",FACE,{"derivedFrom":[makeQuery(id+"F15.boolean.opBoolean","MERGE",FACE,{"derivedFrom":[makeQuery(id+"F12.opExtrude","CAP_FACE",FACE,{"disambiguationData":[OSD([subQ11,sQuery(id+"F5.wireOp",EDGE,"E1"),sQuery(id+"F5.wireOp",EDGE,"E2"),sQuery(id+"F5.wireOp",EDGE,"E3"),sQuery(id+"F5.wireOp",EDGE,"E4"),sQuery(id+"F5.wireOp",EDGE,"E5"),sQuery(id+"F5.wireOp",EDGE,"E6"),sQuery(id+"F5.wireOp",EDGE,"E7"),subQ10,sQuery(id+"F5.wireOp",EDGE,"E10.filletArc"),sQuery(id+"F5.wireOp",EDGE,"E11.filletArc"),subQ9,subQ8,sQuery(id+"F7.wireOp",EDGE,"E14"),sQuery(id+"F7.wireOp",EDGE,"E15"),sQuery(id+"F7.wireOp",EDGE,"E16"),sQuery(id+"F7.wireOp",EDGE,"E17.filletArc"),sQuery(id+"F7.wireOp",EDGE,"E18.filletArc")])],"isStart":false}),makeQuery(id+"F15.opLoft","SWEPT_FACE",FACE,{"disambiguationData":[OSD([subQ11,subQ10,subQ9,subQ8,subQ0,subQ1,subQ3])]})]}),makeQuery(id+"F16.opExtrude","SWEPT_FACE",FACE,{"disambiguationData":[OSD([subQ0,subQ1,subQ3])]})]}),makeQuery(id+"F18.opExtrude","SWEPT_FACE",FACE,{"disambiguationData":[OSD([subQ6])]})]})})]});}
            var Q1;
            {var subQ0=sQuery(id+"F7.wireOp",EDGE,"E18.filletArc");var subQ1=sQuery(id+"F7.wireOp",EDGE,"E17.filletArc");var subQ2=sQuery(id+"F7.wireOp",EDGE,"E16");var subQ3=sQuery(id+"F7.wireOp",EDGE,"E15");var subQ4=sQuery(id+"F7.wireOp",EDGE,"E14");var subQ6=sQuery(id+"F14.wireOp",EDGE,"E20");var subQ7=sQuery(id+"F14.wireOp",EDGE,"E19");var subQ8=sQuery(id+"F5.wireOp",EDGE,"E13.filletArc");var subQ9=sQuery(id+"F5.wireOp",EDGE,"E0");var subQ10=sQuery(id+"F5.wireOp",EDGE,"E1");var subQ11=sQuery(id+"F5.wireOp",EDGE,"E7");var subQ12=sQuery(id+"F5.wireOp",EDGE,"E12.filletArc");var subQ13=sQuery(id+"F5.wireOp",EDGE,"E11.filletArc");var subQ14=sQuery(id+"F5.wireOp",EDGE,"E10.filletArc");var subQ15=sQuery(id+"F5.wireOp",EDGE,"E8");var subQ16=sQuery(id+"F5.wireOp",EDGE,"E6");var subQ17=sQuery(id+"F5.wireOp",EDGE,"E5");var subQ18=sQuery(id+"F5.wireOp",EDGE,"E4");var subQ19=sQuery(id+"F5.wireOp",EDGE,"E3");var subQ20=sQuery(id+"F5.wireOp",EDGE,"E2");var subQ21=sQuery(id+"F14.wireOp",EDGE,"E22");var subQ22=sQuery(id+"F19.wireOp",EDGE,"E39");Q1=makeQuery(id+"F22.opFillet","BLEND_EDGE",EDGE,{"blendedFrom":[makeQuery(id+"F21.boolean.opBoolean","COPY",EDGE,{"derivedFrom":makeQuery(id+"F21.opExtrude","CAP_EDGE",EDGE,{"disambiguationData":[OSD([subQ22])],"isStart":false})}),makeQuery(id+"F21.boolean.opBoolean","SPLIT",FACE,{"disambiguationData":[TD([makeQuery(id+"F6.opRevolve","SWEPT_FACE",FACE,{"disambiguationData":[OSD([subQ10])]})])],"derivedFrom":makeQuery(id+"F18.boolean.opBoolean","MERGE",FACE,{"derivedFrom":[makeQuery(id+"F16.boolean.opBoolean","MERGE",FACE,{"derivedFrom":[makeQuery(id+"F15.boolean.opBoolean","MERGE",FACE,{"derivedFrom":[makeQuery(id+"F12.opExtrude","CAP_FACE",FACE,{"disambiguationData":[OSD([subQ9,subQ10,subQ20,subQ19,subQ18,subQ17,subQ16,subQ11,subQ15,subQ14,subQ13,subQ12,subQ8,subQ4,subQ3,subQ2,subQ1,subQ0])],"isStart":false}),makeQuery(id+"F15.opLoft","SWEPT_FACE",FACE,{"disambiguationData":[OSD([subQ9,subQ15,subQ12,subQ8,subQ7,subQ6,subQ21])]})]}),makeQuery(id+"F16.opExtrude","SWEPT_FACE",FACE,{"disambiguationData":[OSD([subQ7,subQ6,subQ21])]})]}),makeQuery(id+"F18.opExtrude","SWEPT_FACE",FACE,{"disambiguationData":[OSD([sQuery(id+"F17.wireOp",EDGE,"E34")])]})]})})],"blendedInto":[makeQuery(id+"F21.boolean.opBoolean","SPLIT",FACE,{"disambiguationData":[TD([makeQuery(id+"F6.opRevolve","SWEPT_FACE",FACE,{"disambiguationData":[OSD([subQ10])]})])],"derivedFrom":makeQuery(id+"F18.boolean.opBoolean","MERGE",FACE,{"derivedFrom":[makeQuery(id+"F16.boolean.opBoolean","MERGE",FACE,{"derivedFrom":[makeQuery(id+"F15.boolean.opBoolean","MERGE",FACE,{"derivedFrom":[makeQuery(id+"F12.opExtrude","CAP_FACE",FACE,{"disambiguationData":[OSD([subQ9,subQ10,subQ20,subQ19,subQ18,subQ17,subQ16,subQ11,subQ15,subQ14,subQ13,subQ12,subQ8,subQ4,subQ3,subQ2,subQ1,subQ0])],"isStart":false}),makeQuery(id+"F15.opLoft","SWEPT_FACE",FACE,{"disambiguationData":[OSD([subQ9,subQ15,subQ12,subQ8,subQ7,subQ6,subQ21])]})]}),makeQuery(id+"F16.opExtrude","SWEPT_FACE",FACE,{"disambiguationData":[OSD([subQ7,subQ6,subQ21])]})]}),makeQuery(id+"F18.opExtrude","SWEPT_FACE",FACE,{"disambiguationData":[OSD([sQuery(id+"F17.wireOp",EDGE,"E34")])]})]})})]});}
            fillet(context, id + "F32", {"entities" : qUnion([Q0, Q1]), "tangentPropagation" : true, "radius" : 0.5 * mm, "defaultsChanged" : false, "vertexSettings" : []});
        }
    });
